# Revit family: Seating-LAMMHULTS-GRADE-Wooden_frame
name_source: partatom
category: Furniture
revit_build: Autodesk Revit 2014 (Build: 20140709_2115(x64)
units: mm (PartAtom-declared; Revit-internal decimal feet)

## types (3) — shared parameters
Assembly Code = E2020
Depth = 780 mm  [stored 2.55906 ft]
Description = *Please enter mtrl description here for use in mto*
Frame Material = Wood - Solid - Ashtree
Height = 540 mm  [stored 1.77165 ft]
Keynote = 46.B
Manufacturer = LAMMHULTS
Model = GRADE
URL = www.lammhults.se
Weight = 4.7
Width = 480 mm  [stored 1.5748 ft]

## per-type parameters (varying)
| type | Seat Material | Seat Pad Material |
| Ash - Beige | Colour - Coated - Beige | Fabric - Divina 3 - 236 |
| Ash - Blue green | Colour - Coated - Blue green | Fabric - Divina 3 - 384 |
| Ash - Fabric | Fabric - Divina 3 - 856 | Fabric - Divina 3 - 691 |

note: [stored X ft] marks values corroborated as IEEE doubles in the binary element streams (Revit-internal decimal feet)

## geometry (parser evidence)
native form markers: Blend x444, Sweep x1
no freeform markers — native parametric forms only
